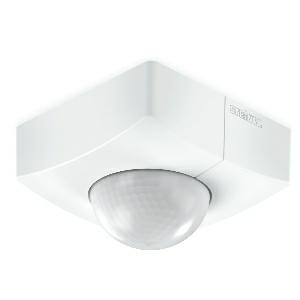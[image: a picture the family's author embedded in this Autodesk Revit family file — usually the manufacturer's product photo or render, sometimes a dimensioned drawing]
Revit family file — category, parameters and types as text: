
# Revit family: is_345_010584
name_source: partatom
category: Elektroinstallationen
revit_build: Autodesk Revit 2016 (Build: 20190508_0715(x64)
units: mm (PartAtom-declared; Revit-internal decimal feet)

## family parameters
Basisbauteil = Fläche
Beim Laden mit Abzugskörper schneiden = Nein
Bemaßung runder Anschluss = Durchmesser verwenden
Beschriftungsausrichtung beibehalten = Nein
Gemeinsam genutzt = Nein
Raumberechnungspunkt = Nein
Teiletyp = Normal

## types (1)
- IS 345
    Apparent Load = 0 VA
    Beschreibung = Type: Motion detectors; Dimensions (L x W x H): 65 x 95 x 95 mm; Mains power supply: 220 – 240 V / 50 – 60 Hz; Sensor Technology: passive infrared; Application, place: Outdoors, Indoors; Application, room: corridor / aisle, multi-storey / underground car park, outdoors, Indoors; Installation site: ceiling; Installation: Surface wiring; Switching zones: 280 switching zones; Electronic scalability: No; Mechanical scalability: No; Mounting height: 2,50 – 5,00 m; Optimum mounting height: 2,8 m; Detection angle: 360 °; Angle of aperture: 45 °; Sneak-by guard: Yes; Capability of masking out individual segments: Yes; Reach, radial: 12 x 6 m (72 m²); Reach, tangential: 23 x 6 m (138 m²); Twilight setting TEACH: Yes; Twilight setting: 2 – 1000 lx; Time setting: 5 sec – 15 min; Control output, Dali: Broadcast 1x30 electronic ballasts; Constant-lighting control: Yes; Basic light level function: Yes; Basic light level function in per cent: 10 – 50 %; Basic light level function time: 1-30 min, all night; Basic light level function percentage, from: 10 %; Basic light level function percentage, up to: 50 %; Functions: Normal / test mode, Manual ON / ON-OFF, Constant-lighting control ON-OFF; Settings via: Remote control, Potentiometers, Smart Remote; With remote control: No; Interconnection: Yes; IP-rating: IP54; Material: Plastic; Ambient temperature: -20 – 50 °C; Colour: white; Colour, RAL: 9003; Manufacturer's Warranty: 5 years; Version: DALI-2 Application Controller - surface, sq.; PU1, EAN: 4007841010584
    Height = 95 mm
    Hersteller = Steinel
    Length = 65 mm
    Maximum range = 11.589 m
    ModVariant = Nein
    Modell = 010584
    Mounting Place = Ceiling
    Mounting Type = Surface mounted
    Number of Poles = 1
    OnlyDefault = Ja
    Power Factor = 1
    Product Name = IS 345
    Product group = Sensor-switched outdoor light
    ProductGroupID = 3
    Protection Class = Protection class
    Protection Degree = IP 54
    RlxData = <blob elided: 164025 chars, md5=e2625fb8>
    Sensor characteristics = Stretched
    Sensor type = Passive (infrared)
    SensorDataFile = <blob elided: 5885 chars, md5=98bccc25>
    Type of entry = Motion
    Typenbild = produkt1_010584.jpg
    Typenkommentare = Product without accessories
    URL = http://relux.com
    VarID = ---
    Voltage = 0 V
    Vorgabe-Ansicht = 1800 mm
    Weight = 0.00 kg
    Width = 95 mm

## geometry (parser evidence)
native form markers: Blend x4, Sweep x12
no freeform markers — native parametric forms only
